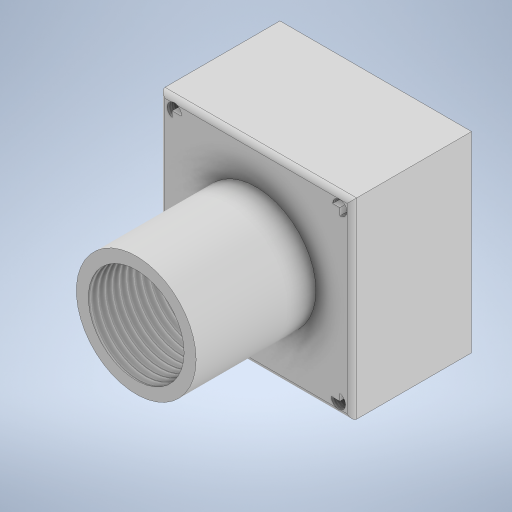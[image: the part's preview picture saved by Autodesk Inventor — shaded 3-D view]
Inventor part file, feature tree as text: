
AUTODESK INVENTOR PART (.ipt)
format: ipt  version: 2024 (Build 280153000, 153)  size: 299,520 bytes
history: native  units: mm
features: sketch x6, thread x5, extrude x4, fillet x1
ambient origin geometry x8: Origin, YZ Plane, XZ Plane, XY Plane, X Axis, Y Axis, Z Axis, Center Point
bodies: Solid1 (feature_tree)
feature tree (16):
  extrude  "Extrusion1"  Depth=80.0mm
  extrude  "Extrusion2"  Depth=50.0mm
  sketch  "3D Sketch1"
  sketch  "Sketch3"  dims[d5=5.0mm d6=50.0mm d7=0.0mm d8=70.0mm d9=70.0mm d10=6.0mm d11=6.0mm d12=6.0mm d13=6.0mm]
  extrude  "Extrusion3"  Depth=50.0mm TaperAngle=0.0deg
  fillet  "Fillet1"  Radius=70.0mm
  thread  "Thread1"  [1 undecoded]
  thread  "Thread2"  [1 undecoded]
  thread  "Thread3"  [1 undecoded]
  thread  "Thread4"  [1 undecoded]
  thread  "Thread5"  [1 undecoded]
  extrude  "Extrusion4"  Depth=50.0mm
  sketch  "Sketch5"  dims[d17=50.0mm d18=0.0mm d19=50.0mm d20=0.0mm d21=50.0mm d22=0.0mm d23=50.0mm d24=0.0mm d25=50.0mm d26=0.0mm d27=20.0mm d28=0.0mm d29=0.5mm d30=0.872665mm]
  sketch  "Sketch1"  dims[d0=80.0mm d1=80.0mm]
  sketch  "Sketch2"  dims[d2=50.0mm d3=0.0mm d4=50.0mm]
  sketch  "Sketch4"  dims[d14=50.0mm d15=0.0mm d16=2.0mm]
note: 5 required parameter values undecoded (feature->parameter linkage not recoverable at this tier; creation-order binding heuristic only, values carry confidence <= 0.55)
